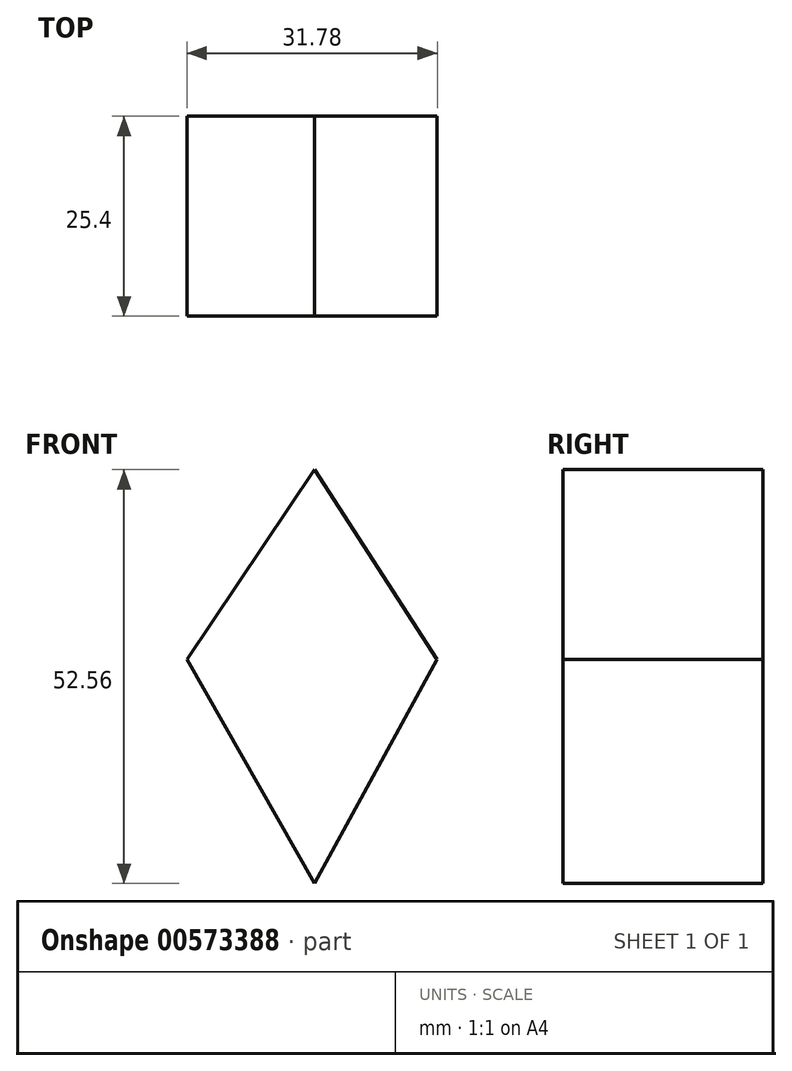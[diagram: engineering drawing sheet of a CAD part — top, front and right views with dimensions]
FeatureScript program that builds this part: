
annotation { "Feature Type Name" : "Feature", "Feature Type Description" : "" }
export const myFeature = defineFeature(function(context is Context, id is Id, definition is map)
    precondition{}
    {
        {
            var Q0;
            Q0=qCreatedBy(makeId("Front.planeOp"),FACE);
            var sketch = newSketch(context, id + "F0", { "sketchPlane" : qUnion([Q0])});
            skLineSegment(sketch, "E0", {"start": v(-60.79, 45.52) * mm, "end": v(-44.6, 17.1) * mm});
            skLineSegment(sketch, "E1", {"start": v(-44.6, 17.1) * mm, "end": v(-29.01, 45.52) * mm});
            skLineSegment(sketch, "E2", {"start": v(-60.79, 45.52) * mm, "end": v(-44.6, 69.66) * mm});
            skLineSegment(sketch, "E3", {"start": v(-44.6, 69.66) * mm, "end": v(-29.01, 45.52) * mm});
            skLineSegment(sketch, "E4", {"start": v(-44.6, 17.1) * mm, "end": v(-54.68, 0) * mm});
            skLineSegment(sketch, "E5", {"start": v(-44.6, 17.1) * mm, "end": v(-32.37, 0) * mm});
            skSolve(sketch);
        }
        {
            var Q0;
            Q0=makeQuery(id+"F0.imprint","IMPRINT",FACE,{"disambiguationData":[TD([[makeQuery(id+"F0.imprint","IMPRINT",EDGE,{"derivedFrom":sQuery(id+"F0.wireOp",EDGE,"E0")}),1.0]])]});
            extrude(context, id + "F1", {"entities" : qUnion([Q0]), "depth" : 25.4 * mm, "offsetDistance" : 25.4 * mm});
        }
    });
